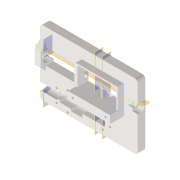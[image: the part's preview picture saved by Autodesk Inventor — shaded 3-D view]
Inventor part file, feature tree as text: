
AUTODESK INVENTOR PART (.ipt)
format: ipt  version: 2022 (Build 260153000, 153)  size: 454,144 bytes
history: native  units: mm
features: sketch x21, extrude x20, reference x11, other x10, plane x8, projected_geometry x8, fillet x2, chamfer x1, mirror x1, hole x1
ambient origin geometry x8: Origin, YZ Plane, XZ Plane, XY Plane, X Axis, Y Axis, Z Axis, Center Point
bodies: Solid1 (feature_tree)
feature tree (83):
  extrude  "Extrusion1"  Depth=10.0mm
  fillet  "Fillet1"  Radius=10.0mm
  extrude  "Extrusion2"  Depth=4.0mm
  extrude  "Extrusion3"  Depth=20.0mm
  plane  "Work Plane1"
  plane  "Work Plane2"
  chamfer  "Chamfer1"  [1 undecoded]
  extrude  "Extrusion4"  Depth=10.0mm
  extrude  "Extrusion5"  Depth=8.0mm
  extrude  "Extrusion6"  Depth=5.0mm TaperAngle=0.0deg
  plane  "Work Plane3"
  extrude  "Extrusion12"  Depth=18.0mm TaperAngle=0.0deg
  extrude  "Extrusion13"  Depth=2.0mm
  mirror  "Mirror1"
  plane  "Work Plane4"
  plane  "Work Plane5"
  extrude  "Extrusion21"  Depth=2.0mm
  extrude  "Extrusion22"  Depth=12.0mm
  plane  "Arbeitsebene7"
  extrude  "Extrusion27"  Depth=7.0mm
  extrude  "Extrusion28"  Depth=10.0mm
  extrude  "Extrusion29"  Depth=2.8mm
  fillet  "Rundung6"  Radius=6.0mm
  sketch  "Skizze32"  dims[d61=30.0mm d62=-0.523599mm d63=12.0mm]
  plane  "Arbeitsebene8"
  extrude  "Extrusion30"  TaperAngle=0.0deg  [1 undecoded]
  extrude  "Extrusion31"  Depth=40.0mm TaperAngle=0.0deg
  extrude  "Extrusion32"  Depth=8.0mm
  extrude  "Extrusion33"  Depth=2.0mm
  sketch  "Skizze36"  dims[d108=6.0mm d109=0.0mm d110=0.0mm]
  plane  "Arbeitsebene9"
  extrude  "Extrusion34"  TaperAngle=45.0deg  [1 undecoded]
  extrude  "Extrusion35"  TaperAngle=45.0deg  [1 undecoded]
  hole  "Bohrung2"  [1 undecoded]
  extrude  "Extrusion36"  Depth=8.0mm
  sketch  "Sketch1"  dims[d0=127.8mm d1=85.5mm d2=10.0mm d3=0.0mm]
  sketch  "Sketch2"  dims[d4=4.0mm d5=51.0mm]
  projected_geometry  "Projected Loop1"
  sketch  "Sketch3"  dims[d6=25.0mm d7=20.0mm]
  projected_geometry  "Projected Loop2"
  sketch  "Sketch4"  dims[d8=15.0mm]
  projected_geometry  "Projected Loop3"
  sketch  "Sketch5"  dims[d9=6.0mm]
  sketch  "Sketch6"  dims[d10=0.0mm]
  reference  "Reference2"
  sketch  "Sketch12"  dims[d11=1.5mm d12=0.0mm d13=0.0mm]
  reference  "Reference4"
  sketch  "Sketch13"  dims[d14=4.0mm d15=2.0mm d16=45.0deg d17=10.0mm]
  sketch  "Sketch22"  dims[d18=8.0mm d19=0.0mm d20=1.9mm]
  projected_geometry  "Projected Loop8"
  sketch  "Sketch23"  dims[d21=4.0mm d22=5.0mm d23=0.0mm]
  projected_geometry  "Projected Loop9"
  reference  "Reference11"
  sketch  "Skizze28"  dims[d27=20.0mm d28=18.0mm d29=0.0mm]
  sketch  "Skizze29"  dims[d38=10.0mm d52=2.0mm]
  reference  "Referenz13"
  sketch  "Skizze30"  dims[d53=2.0mm d54=2.0mm]
  reference  "Referenz14"
  reference  "Referenz16"
  sketch  "Skizze33"  dims[d64=7.0mm d65=0.0mm d100=7.0mm]
  reference  "Referenz17"
  sketch  "Skizze34"  dims[d101=10.0mm d102=0.0mm d103=11.8mm]
  reference  "Referenz18"
  sketch  "Skizze35"  dims[d105=2.8mm d106=2.8mm d107=6.0mm]
  projected_geometry  "Projizierte Kontur15"
  reference  "Referenz19"
  reference  "Referenz20"
  sketch  "Skizze37"  dims[d142=0.5mm d143=40.0mm d144=0.0mm]
  reference  "Referenz21"
  sketch  "Skizze38"  dims[d145=8.0mm d146=0.0mm d147=0.5mm]
  projected_geometry  "Projizierte Kontur16"
  sketch  "Skizze39"  dims[d148=1.0mm d149=0.0mm d150=2.0mm d151=45.0deg d152=45.0deg d153=8.0mm d154=0.0mm d155=7.0mm d156=3.0mm d157=0.0mm d158=30.0mm d159=0.0mm d160=17.0mm d161=15.0mm d162=0.0mm d163=0.5mm d164=15.0mm d165=0.0mm d166=8.0mm d167=10.0mm d168=0.0mm d169=2.8mm d170=6.0mm d171=4.0mm d172=2.0mm d173=90.0deg d174=8.0mm d175=20.594885mm d176=0.0mm d177=0.0mm]
  projected_geometry  "Projizierte Kontur17"
  other  "<userpath>\Documents\GitHub\Guinardia\INVENTOR\Assembly_Guinardia_V1.iam"
  other  "Assembly_Guinardia_V1.iam"
  other  "00_CCTV_lens_M12_25mm_5mp:1"
  other  "00_PipetteTip200ul-1:2"
  other  "00_NEMA8:1"
  other  "00_SM05FC2-Step:1"
  other  "00_CCTV_lens_M12_25mm_5mp:2"
  other  "00_HuaweiP30_Telelens_prismonly:1"
  other  "<userpath>\Documents\Inventor\Guinardia\INVENTOR\Assembly_Guinardia_V0.iam"
  other  "Assembly_Guinardia_V0.iam"
note: 5 required parameter values undecoded (feature->parameter linkage not recoverable at this tier; creation-order binding heuristic only, values carry confidence <= 0.55)
